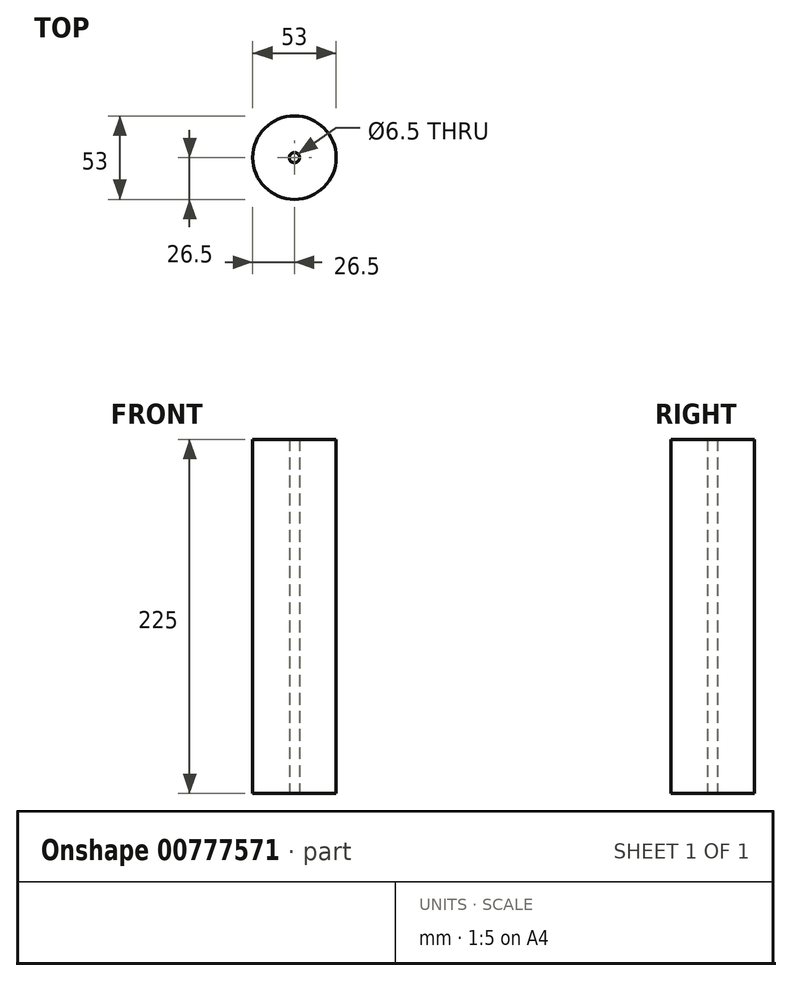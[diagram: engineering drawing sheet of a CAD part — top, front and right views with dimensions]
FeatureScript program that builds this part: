
annotation { "Feature Type Name" : "Feature", "Feature Type Description" : "" }
export const myFeature = defineFeature(function(context is Context, id is Id, definition is map)
    precondition{}
    {
        {
            var Q0;
            Q0=qCreatedBy(makeId("Top.planeOp"),FACE);
            var sketch = newSketch(context, id + "F0", { "sketchPlane" : qUnion([Q0])});
            skCircle(sketch, "E0", {"center": v(0, 0) * mm, "radius": 26.5 * mm});
            skCircle(sketch, "E1", {"center": v(0, 0) * mm, "radius": 3.25 * mm});
            skSolve(sketch);
        }
        {
            var Q0;
            Q0=makeQuery(id+"F0.imprint","IMPRINT",FACE,{"disambiguationData":[TD([[makeQuery(id+"F0.imprint","IMPRINT",EDGE,{"derivedFrom":sQuery(id+"F0.wireOp",EDGE,"E0")}),1.0]])]});
            extrude(context, id + "F1", {"entities" : qUnion([Q0]), "depth" : 225 * mm, "offsetDistance" : 25 * mm});
        }
    });
